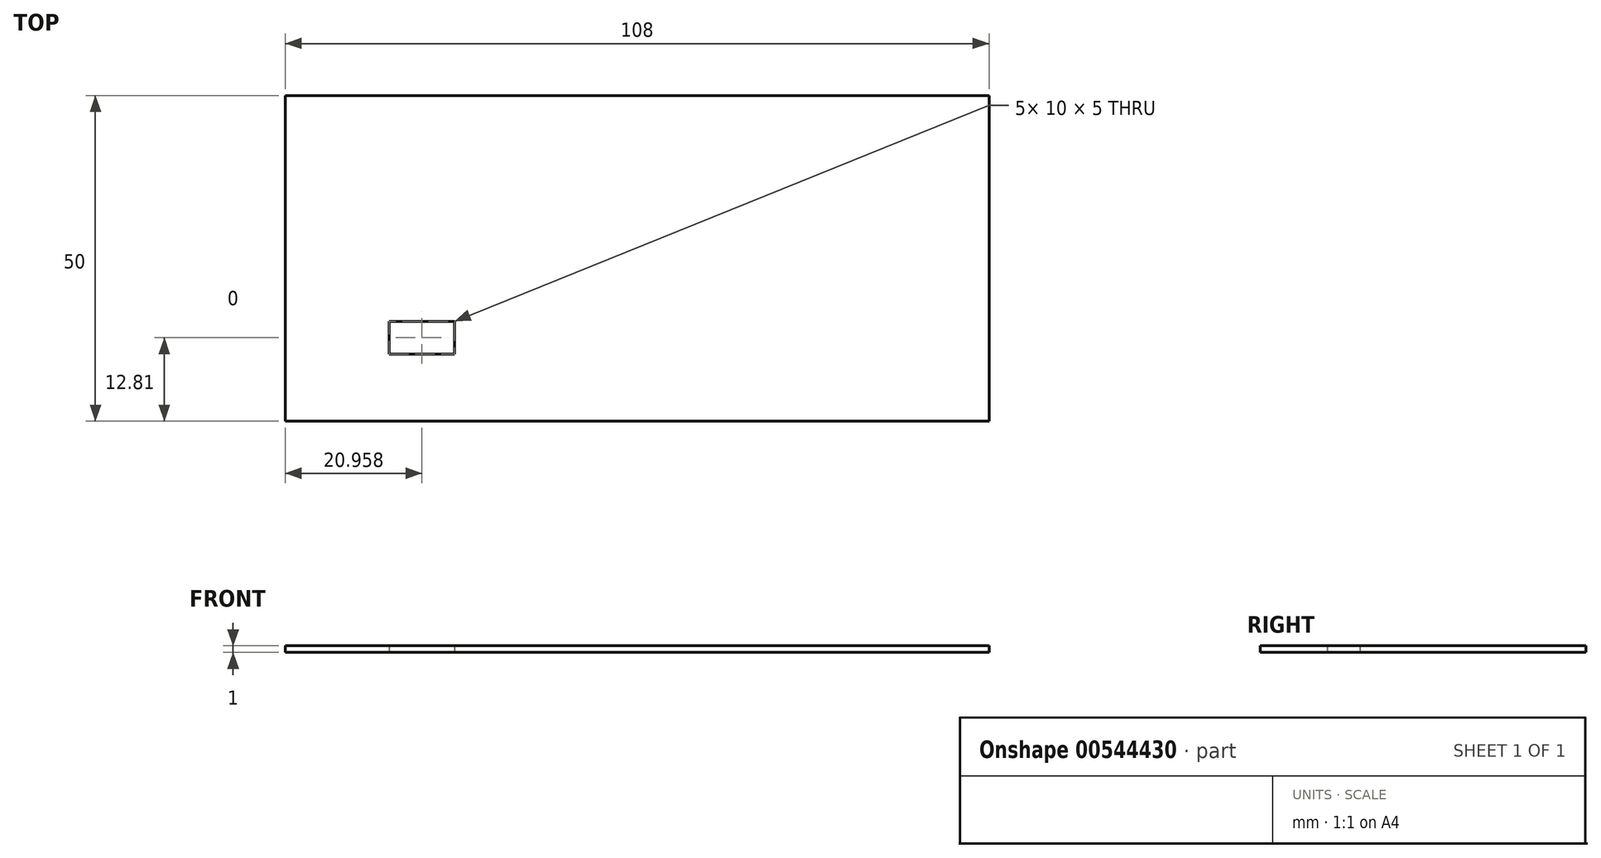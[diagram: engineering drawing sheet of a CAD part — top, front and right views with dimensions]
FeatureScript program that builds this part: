
annotation { "Feature Type Name" : "Feature", "Feature Type Description" : "" }
export const myFeature = defineFeature(function(context is Context, id is Id, definition is map)
    precondition{}
    {
        {
            var Q0;
            Q0=qCreatedBy(makeId("Top.planeOp"),FACE);
            var sketch = newSketch(context, id + "F0", { "sketchPlane" : qUnion([Q0])});
            skLineSegment(sketch, "E0.bottom", {"start": v(55.48, 39.69) * mm, "end": v(-52.52, 39.69) * mm});
            skLineSegment(sketch, "E0.top", {"start": v(55.48, -10.31) * mm, "end": v(-52.52, -10.31) * mm});
            skLineSegment(sketch, "E0.left", {"start": v(55.48, 39.69) * mm, "end": v(55.48, -10.31) * mm});
            skLineSegment(sketch, "E0.right", {"start": v(-52.52, 39.69) * mm, "end": v(-52.52, -10.31) * mm});
            skLineSegment(sketch, "E1.bottom", {"start": v(-26.56, 5) * mm, "end": v(-36.56, 5) * mm});
            skLineSegment(sketch, "E1.top", {"start": v(-26.56, 0) * mm, "end": v(-36.56, 0) * mm});
            skLineSegment(sketch, "E1.left", {"start": v(-26.56, 5) * mm, "end": v(-26.56, 0) * mm});
            skLineSegment(sketch, "E1.right", {"start": v(-36.56, 5) * mm, "end": v(-36.56, 0) * mm});
            skSolve(sketch);
        }
        {
            var Q0;
            Q0=makeQuery(id+"F0.imprint","IMPRINT",FACE,{"disambiguationData":[TD([[makeQuery(id+"F0.imprint","IMPRINT",EDGE,{"derivedFrom":sQuery(id+"F0.wireOp",EDGE,"E0.bottom")}),1.0]])]});
            extrude(context, id + "F1", {"entities" : qUnion([Q0]), "depth" : 1 * mm, "offsetDistance" : 25 * mm});
        }
    });
